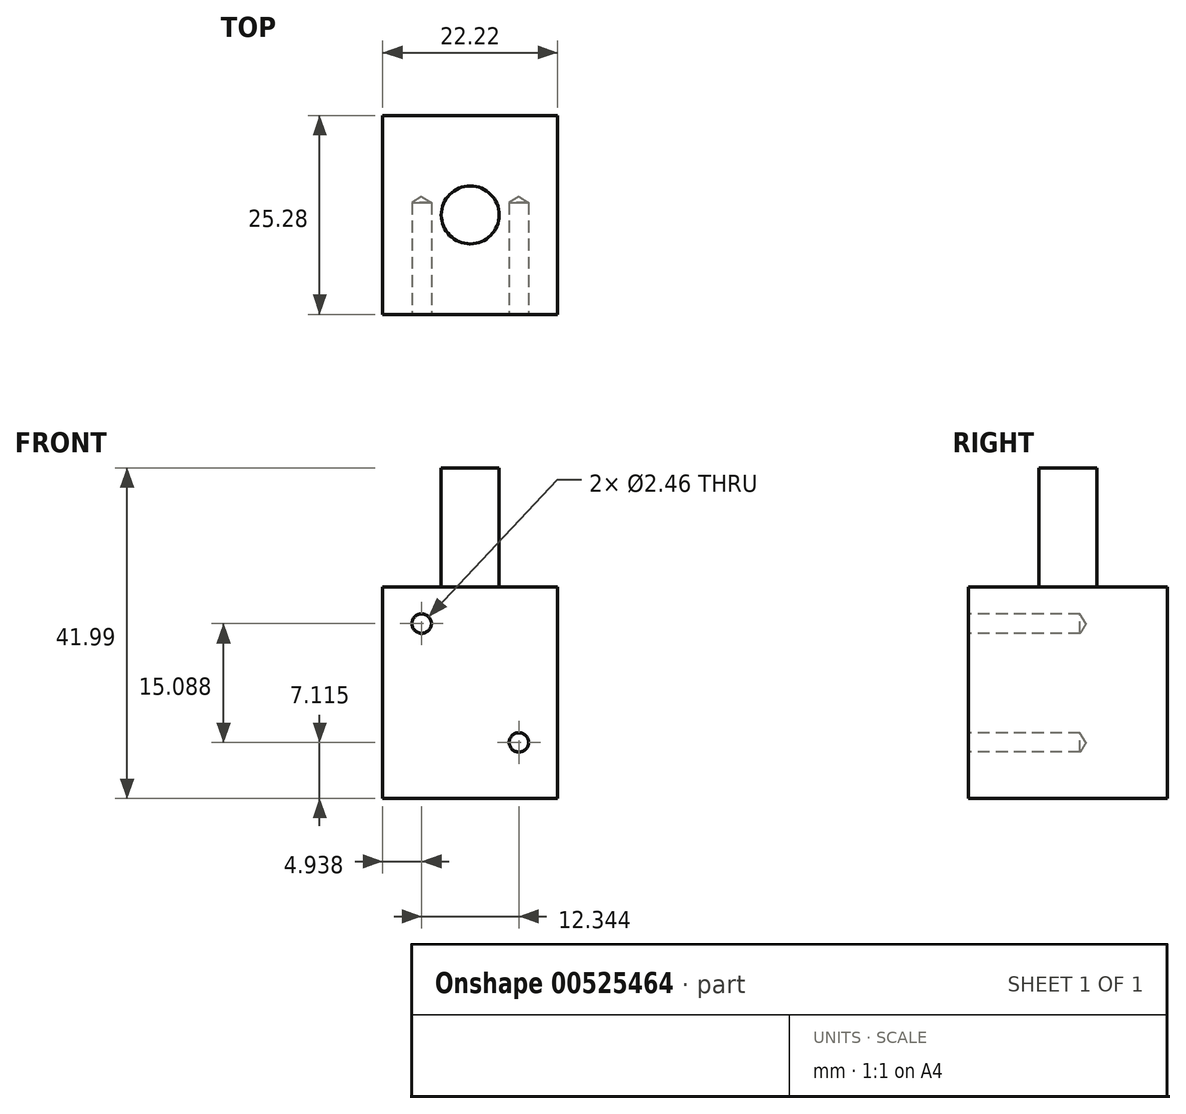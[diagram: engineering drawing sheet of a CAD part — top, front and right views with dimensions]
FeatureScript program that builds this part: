
annotation { "Feature Type Name" : "Feature", "Feature Type Description" : "" }
export const myFeature = defineFeature(function(context is Context, id is Id, definition is map)
    precondition{}
    {
        {
            var Q0;
            Q0=qCreatedBy(makeId("Front.planeOp"),FACE);
            var sketch = newSketch(context, id + "F0", { "sketchPlane" : qUnion([Q0])});
            skLineSegment(sketch, "E0.bottom", {"start": v(11.11, 13.44) * mm, "end": v(-11.11, 13.44) * mm});
            skLineSegment(sketch, "E0.top", {"start": v(11.11, -13.44) * mm, "end": v(-11.11, -13.44) * mm});
            skLineSegment(sketch, "E0.left", {"start": v(11.11, 13.44) * mm, "end": v(11.11, -13.44) * mm});
            skLineSegment(sketch, "E0.right", {"start": v(-11.11, 13.44) * mm, "end": v(-11.11, -13.44) * mm});
            skPoint(sketch, "E0.middle", {"position": v(0, 0) * mm});
            skSolve(sketch);
        }
        {
            var Q0;
            Q0 = qSketchRegion(id + "F0", true);
            extrude(context, id + "F1", {"entities" : qUnion([Q0]), "endBound" : BoundingType.SYMMETRIC, "depth" : 25.27 * mm, "offsetDistance" : 25.4 * mm});
        }
        {
            var Q0;
            Q0=makeQuery(id+"F1.opExtrude","SWEPT_FACE",FACE,{"disambiguationData":[OSD([sQuery(id+"F0.wireOp",EDGE,"E0.bottom")])]});
            var sketch = newSketch(context, id + "F2", { "sketchPlane" : qUnion([Q0])});
            skCircle(sketch, "E1", {"center": v(0, 0) * mm, "radius": 3.68 * mm});
            skSolve(sketch);
        }
        {
            var Q0;
            Q0 = qSketchRegion(id + "F2", true);
            extrude(context, id + "F3", {"entities" : qUnion([Q0]), "operationType" : NewBodyOperationType.ADD, "depth" : 15.1 * mm, "offsetDistance" : 25.4 * mm});
        }
        {
            var Q0;
            Q0=makeQuery(id+"F1.opExtrude","CAP_FACE",FACE,{"disambiguationData":[OSD([sQuery(id+"F0.wireOp",EDGE,"E0.bottom"),sQuery(id+"F0.wireOp",EDGE,"E0.top"),sQuery(id+"F0.wireOp",EDGE,"E0.left"),sQuery(id+"F0.wireOp",EDGE,"E0.right")])],"isStart":false});
            var sketch = newSketch(context, id + "F4", { "sketchPlane" : qUnion([Q0])});
            skLineSegment(sketch, "E2.bottom", {"start": v(6.17, 8.76) * mm, "end": v(-6.17, 8.76) * mm});
            skLineSegment(sketch, "E2.top", {"start": v(6.17, -6.32) * mm, "end": v(-6.17, -6.32) * mm});
            skLineSegment(sketch, "E2.left", {"start": v(6.17, 8.76) * mm, "end": v(6.17, -6.32) * mm});
            skLineSegment(sketch, "E2.right", {"start": v(-6.17, 8.76) * mm, "end": v(-6.17, -6.32) * mm});
            skPoint(sketch, "E2.middle", {"position": v(0, 1.22) * mm});
            skSolve(sketch);
        }
        {
            var Q0;
            Q0=sQuery(id+"F4.wireOp",VERTEX,"E2.right.start");
            var Q1;
            Q1=sQuery(id+"F4.wireOp",VERTEX,"E2.left.end");
            var Q2;
            Q2=makeQuery(id+"F1.opExtrude","SWEPT_BODY",BODY,{"disambiguationData":[OSD([sQuery(id+"F0.wireOp",EDGE,"E0.bottom"),sQuery(id+"F0.wireOp",EDGE,"E0.top"),sQuery(id+"F0.wireOp",EDGE,"E0.left"),sQuery(id+"F0.wireOp",EDGE,"E0.right")])]});
            hole(context, id + "F5", {"style" : HoleStyle.SIMPLE, "endStyle" : HoleEndStyle.BLIND, "holeDiameter" : 2.46 * mm, "holeDepth" : 14.2 * mm, "isTappedThrough" : true, "tappedDepth" : 12.7 * mm, "tapClearance" : 3, "startFromSketch" : true, "locations" : qUnion([Q0, Q1]), "scope" : qUnion([Q2])});
        }
    });
